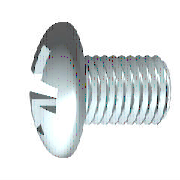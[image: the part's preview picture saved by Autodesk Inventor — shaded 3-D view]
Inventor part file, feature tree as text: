
AUTODESK INVENTOR PART (.ipt)
format: ipt  version: 2022 (Build 260153000, 153)  size: 284,672 bytes
history: native  units: mm (DEFAULTED — no unit token found)
features: other x2, plane x2, extrude x1
ambient origin geometry x7: Origin, YZ Plane, XZ Plane, X Axis, Y Axis, Z Axis, Center Point
bodies: Solid1 (feature_tree)
feature tree (5):
  other  "Базовый элемент"
  plane  "Work Plane1"
  extrude  "Паз"  Depth=4.0mm
  other  "Вырез"
  plane  "Work Plane3"
